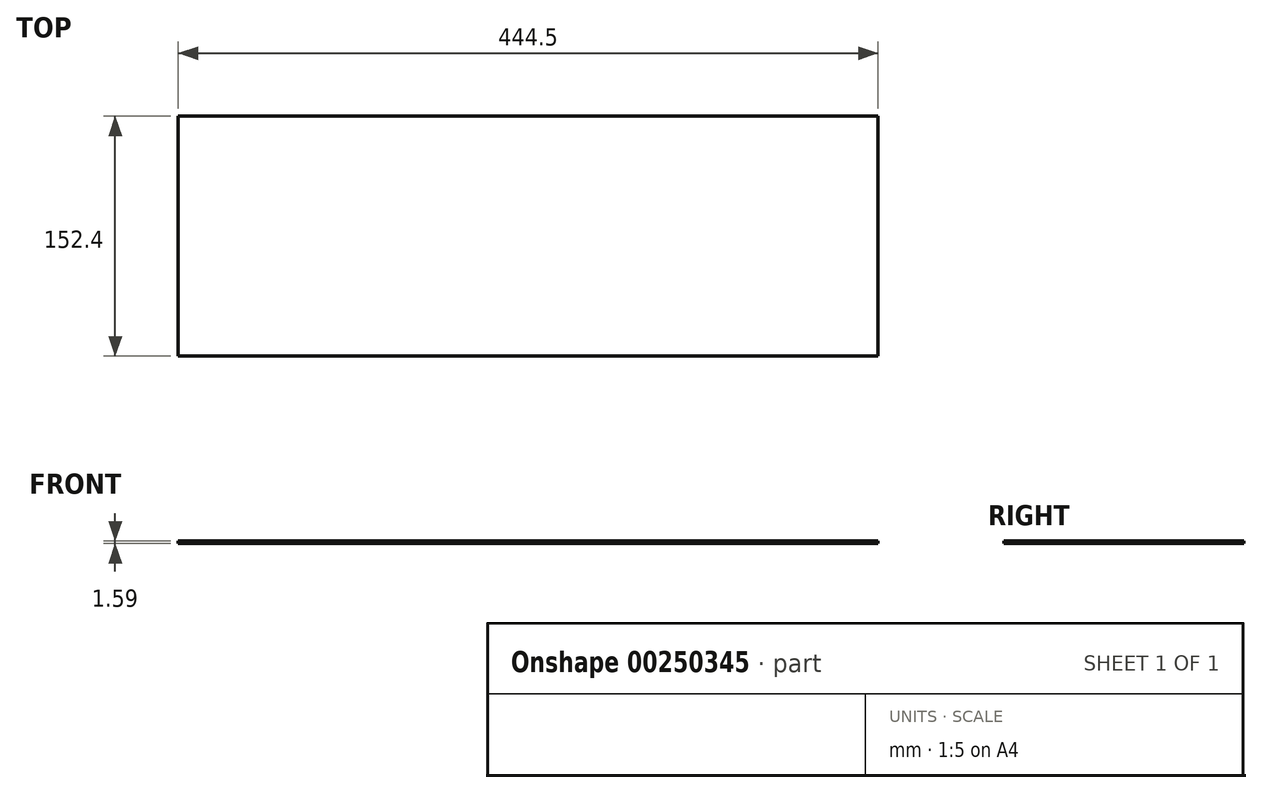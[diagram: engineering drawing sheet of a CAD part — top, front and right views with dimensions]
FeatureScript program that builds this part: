
annotation { "Feature Type Name" : "Feature", "Feature Type Description" : "" }
export const myFeature = defineFeature(function(context is Context, id is Id, definition is map)
    precondition{}
    {
        {
            var Q0;
            Q0=qCreatedBy(makeId("Top.planeOp"),FACE);
            var sketch = newSketch(context, id + "F0", { "sketchPlane" : qUnion([Q0])});
            skLineSegment(sketch, "E0.bottom", {"start": v(222.25, 76.2) * mm, "end": v(-222.25, 76.2) * mm});
            skLineSegment(sketch, "E0.top", {"start": v(222.25, -76.2) * mm, "end": v(-222.25, -76.2) * mm});
            skLineSegment(sketch, "E0.left", {"start": v(222.25, 76.2) * mm, "end": v(222.25, -76.2) * mm});
            skLineSegment(sketch, "E0.right", {"start": v(-222.25, 76.2) * mm, "end": v(-222.25, -76.2) * mm});
            skPoint(sketch, "E0.middle", {"position": v(0, 0) * mm});
            skSolve(sketch);
        }
        {
            var Q0;
            Q0 = qSketchRegion(id + "F0", true);
            extrude(context, id + "F1", {"entities" : qUnion([Q0]), "depth" : 1.59 * mm});
        }
    });
